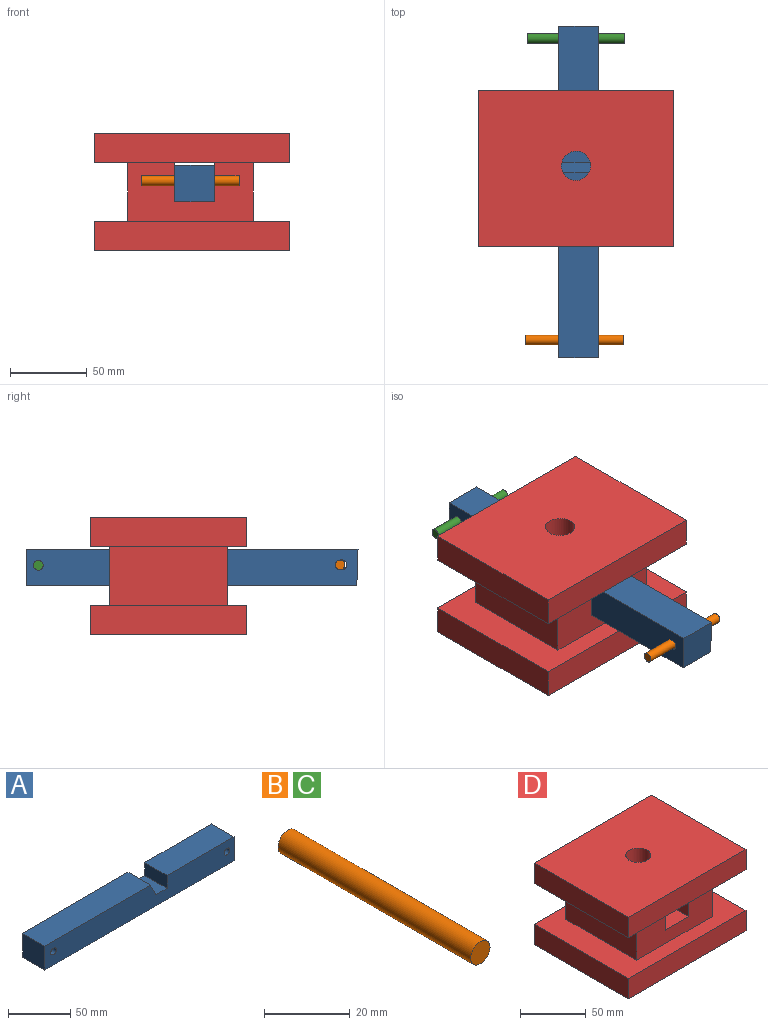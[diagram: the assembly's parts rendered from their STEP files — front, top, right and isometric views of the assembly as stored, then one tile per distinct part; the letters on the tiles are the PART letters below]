
ASSEMBLY  parts=4 mates=2
PART A: 12 faces, bbox 215.9x25.4x23.8 mm
  f0: plane 76.2x25.4mm, normal (0,0,1), area 1935.5mm2, adj f1,f2,f5,f10
  f1: plane 215.9x23.81mm, normal (0,-1,0), area 4866.9mm2, adj f0,f3,f4,f5,f6,f7,f8,f9
  f2: plane 215.9x23.81mm, normal (0,1,0), area 4866.9mm2, adj f0,f3,f4,f5,f6,f7,f8,f9
  f3: plane 25.4x23.81mm, normal (-1,0,-0.03), area 605.2mm2, adj f1,f2,f4,f6
  f4: plane 215.12x25.4mm, normal (0,0,-1), area 5464.1mm2, adj f1,f2,f3,f5
  f5: plane 25.4x23.81mm, normal (1,0,0), area 604.8mm2, adj f0,f1,f2,f4
  f6: plane 120.65x25.4mm, normal (0,0,1), area 3064.5mm2, adj f1,f2,f3,f8
  f7: cylinder r=3.17mm len=25.4mm, axis (0,-1,0), area 506.7mm2, adj f1,f2
  f8: plane 25.4x12.7mm, normal (0.89,0,0.45), area 360.7mm2, adj f1,f2,f6,f9
  f9: plane 25.4x12.7mm, normal (0,0,1), area 322.6mm2, adj f1,f2,f8,f10
  f10: plane 25.4x12.7mm, normal (-1,0,0), area 322.6mm2, adj f0,f1,f2,f9
  f11: cylinder r=3.17mm len=25.4mm, axis (0,-1,0), area 506.7mm2, adj f1,f2
PART B: 3 faces, bbox 6.4x63.5x6.4 mm
  f0: cylinder r=3.17mm len=63.5mm, axis (0,1,0), area 1266.8mm2, adj f1,f2
  f1: plane 6.35x6.35mm, normal (0,-1,0), area 31.7mm2, adj f0
  f2: plane 6.35x6.35mm, normal (0,1,0), area 31.7mm2, adj f0
PART C: same geometry as B
PART D: 20 faces, bbox 127x101.6x76.2 mm
  f0: plane 76.2x25.4mm, normal (1,0,0), area 1935.5mm2, adj f4,f8,f18,f19
  f1: plane 76.2x25.4mm, normal (-1,0,0), area 1935.5mm2, adj f4,f8,f18,f19
  f2: plane 76.2x38.1mm, normal (1,0,0), area 2903.2mm2, adj f8,f12,f18,f19
  f3: plane 76.2x38.1mm, normal (-1,0,0), area 2903.2mm2, adj f8,f12,f18,f19
  f4: plane 76.2x25.4mm, normal (0,0,1), area 1935.5mm2, adj f0,f1,f18,f19
  f5: plane 127x19.05mm, normal (0,-1,0), area 2419.4mm2, adj f8,f9,f10,f11
  f6: plane 127x19.05mm, normal (0,1,0), area 2419.3mm2, adj f12,f13,f14,f15
  f7: plane 127x19.05mm, normal (0,1,0), area 2419.3mm2, adj f8,f9,f10,f11
  f8: plane 127x101.6mm, normal (0,0,-1), area 8337.1mm2, adj f0,f1,f2,f3,f5,f7,f9,f11
  f9: plane 101.6x19.05mm, normal (1,0,0), area 1935.5mm2, adj f5,f7,f8,f10
  f10: plane 127x101.6mm, normal (0,0,1), area 12618.2mm2, adj f5,f7,f9,f11,f17
  f11: plane 101.6x19.05mm, normal (-1,0,0), area 1935.5mm2, adj f5,f7,f8,f10
  f12: plane 127x101.6mm, normal (0,0,1), area 6686.6mm2, adj f2,f3,f6,f13,f15,f16,f18,f19
  f13: plane 101.6x19.05mm, normal (-1,0,0), area 1935.5mm2, adj f6,f12,f14,f16
  f14: plane 127x101.6mm, normal (0,0,-1), area 12903.2mm2, adj f6,f13,f15,f16
  f15: plane 101.6x19.05mm, normal (1,0,0), area 1935.5mm2, adj f6,f12,f14,f16
  f16: plane 127x19.05mm, normal (0,-1,0), area 2419.3mm2, adj f12,f13,f14,f15
  f17: cylinder r=9.53mm len=19.05mm, axis (0,0,1), area 1140.1mm2, adj f8,f10
  f18: plane 81.58x38.1mm, normal (0,1,0), area 2463.1mm2, adj f0,f1,f2,f3,f4,f8,f12
  f19: plane 81.58x38.1mm, normal (0,-1,0), area 2463.1mm2, adj f0,f1,f2,f3,f4,f8,f12
PLACE A rot(axis=(0,0,1),90deg) t=(-108.47,-195.27,-79.05)mm
PLACE B rot(axis=(0.58,-0.58,0.58),120deg) t=(-130.32,-296.7,-13.6)mm fixed
PLACE C rot(axis=(0.58,0.58,-0.58),120deg) t=(-65.6,-100.49,-77.65)mm fixed
PLACE D t=(-101.49,-104.85,-73.23)mm fixed
MATE slider A.f5 <-> D.f18  axis (0,1,0) through (-83.07,-62.94,-59.07)mm
MATE slider C.f0 <-> A.f7  axis (1,0,0) through (-65.6,-70.98,-45.78)mm
